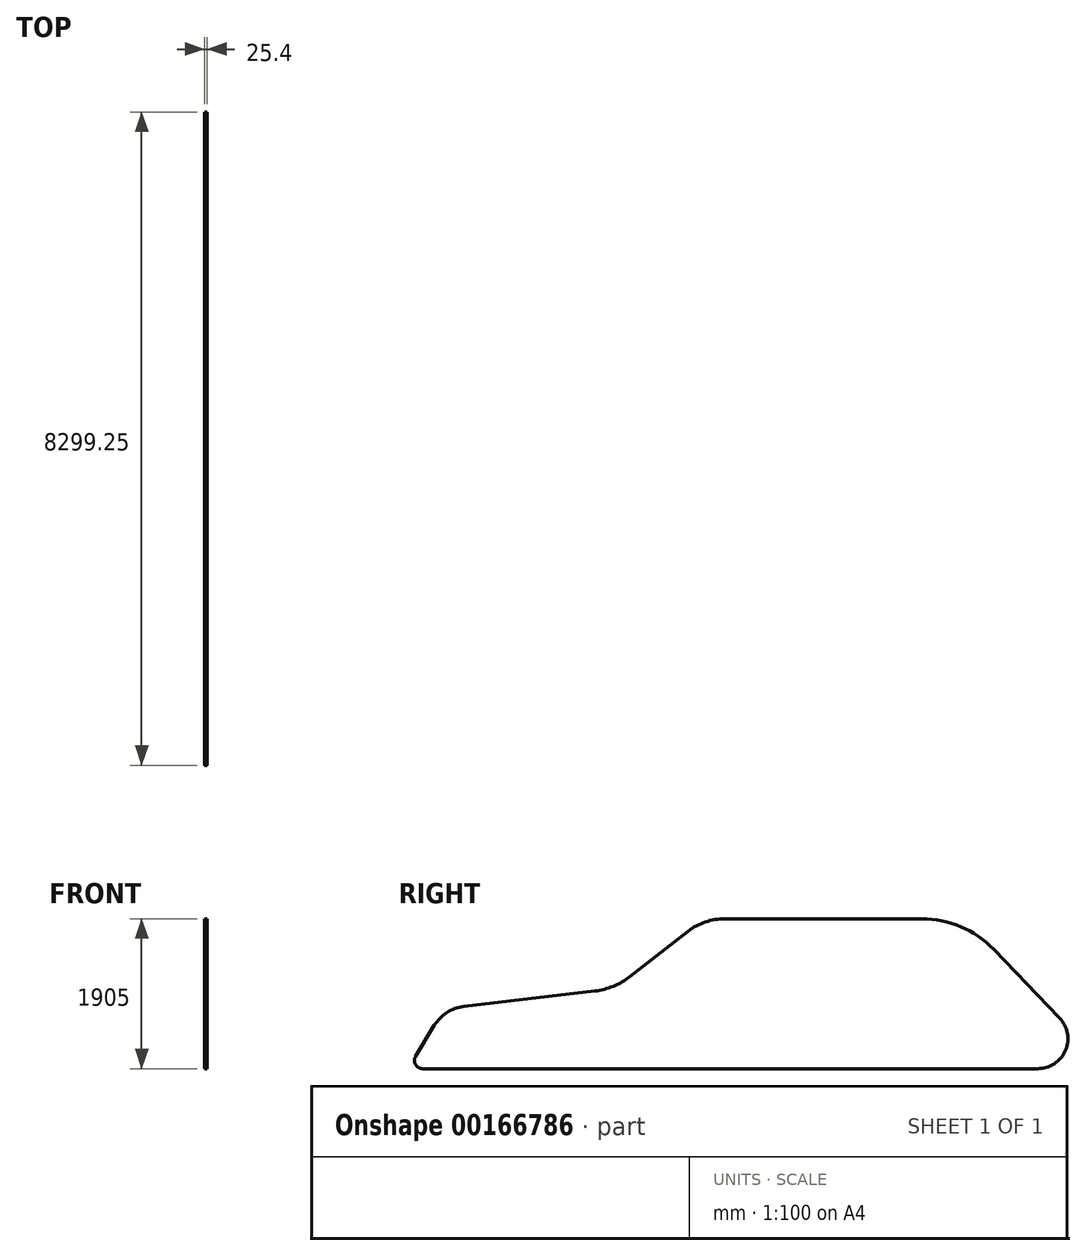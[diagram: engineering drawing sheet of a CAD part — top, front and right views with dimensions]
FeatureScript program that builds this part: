
annotation { "Feature Type Name" : "Feature", "Feature Type Description" : "" }
export const myFeature = defineFeature(function(context is Context, id is Id, definition is map)
    precondition{}
    {
        {
            var Q0;
            Q0=qCreatedBy(makeId("Front.planeOp"),FACE);
            var sketch = newSketch(context, id + "F0", { "sketchPlane" : qUnion([Q0])});
            skLineSegment(sketch, "E0", {"start": v(0, -1143) * mm, "end": v(1407.05, -1143) * mm, "construction": true});
            skLineSegment(sketch, "E1", {"start": v(494.4, 0) * mm, "end": v(1594.53, 0) * mm});
            skLineSegment(sketch, "E2.top", {"start": v(1109.62, -621.68) * mm, "end": v(1389.02, -621.68) * mm});
            skPoint(sketch, "E3.visualSharp", {"position": v(1057.47, -621.68) * mm});
            skLineSegment(sketch, "E4", {"start": v(1058.82, -529.74) * mm, "end": v(1058.82, -570.88) * mm});
            skPoint(sketch, "E5.visualSharp", {"position": v(1058.82, -621.68) * mm});
            skArc(sketch, "E5.filletArc", {"start": v(1058.82, -570.88) * mm, "mid": v(1073.7, -606.8) * mm, "end": v(1109.62, -621.68) * mm});
            skLineSegment(sketch, "E6", {"start": v(1439.82, -570.88) * mm, "end": v(1439.82, -529.74) * mm});
            skPoint(sketch, "E7.visualSharp", {"position": v(1439.82, -621.68) * mm});
            skArc(sketch, "E7.filletArc", {"start": v(1389.02, -621.68) * mm, "mid": v(1424.94, -606.8) * mm, "end": v(1439.82, -570.88) * mm});
            skPoint(sketch, "E8.visualSharp", {"position": v(1058.82, -489.77) * mm});
            skArc(sketch, "E9.filletArc", {"start": v(1109.62, -478.94) * mm, "mid": v(1073.7, -493.81) * mm, "end": v(1058.82, -529.74) * mm});
            skPoint(sketch, "E10.visualSharp", {"position": v(1439.82, -489.77) * mm});
            skArc(sketch, "E10.filletArc", {"start": v(1439.82, -529.74) * mm, "mid": v(1424.94, -493.81) * mm, "end": v(1389.02, -478.94) * mm});
            skArc(sketch, "E11", {"start": v(1389.02, -478.94) * mm, "mid": v(1249.32, -469.28) * mm, "end": v(1109.62, -478.94) * mm});
            skSolve(sketch);
        }
        {
            var Q0;
            Q0=qCreatedBy(makeId("Right.planeOp"),FACE);
            var sketch = newSketch(context, id + "F1", { "sketchPlane" : qUnion([Q0])});
            skLineSegment(sketch, "E12", {"start": v(179.44, 0) * mm, "end": v(7996.1, 0) * mm});
            skLineSegment(sketch, "E13", {"start": v(92.32, 153.87) * mm, "end": v(328.8, 548) * mm});
            skPoint(sketch, "E14.visualSharp", {"position": v(0, 0) * mm});
            skArc(sketch, "E14.filletArc", {"start": v(92.32, 153.87) * mm, "mid": v(91.03, 51.54) * mm, "end": v(179.44, 0) * mm});
            skLineSegment(sketch, "E15", {"start": v(705.05, 791.16) * mm, "end": v(2369.98, 987.03) * mm});
            skPoint(sketch, "E16.visualSharp", {"position": v(457.2, 762) * mm});
            skArc(sketch, "E16.filletArc", {"start": v(705.05, 791.16) * mm, "mid": v(488.68, 713.3) * mm, "end": v(328.8, 548) * mm});
            skLineSegment(sketch, "E17", {"start": v(2811.9, 1168.2) * mm, "end": v(3552.83, 1744.49) * mm});
            skPoint(sketch, "E18.visualSharp", {"position": v(2616.2, 1016) * mm});
            skArc(sketch, "E18.filletArc", {"start": v(2369.98, 987.03) * mm, "mid": v(2603.33, 1047.39) * mm, "end": v(2811.9, 1168.2) * mm});
            skLineSegment(sketch, "E19", {"start": v(4020.65, 1905) * mm, "end": v(6519.9, 1905) * mm});
            skPoint(sketch, "E20.visualSharp", {"position": v(3759.2, 1905) * mm});
            skArc(sketch, "E20.filletArc", {"start": v(4020.65, 1905) * mm, "mid": v(3773.35, 1863.76) * mm, "end": v(3552.83, 1744.49) * mm});
            skLineSegment(sketch, "E21", {"start": v(7436.07, 1514.52) * mm, "end": v(8270.94, 644.85) * mm});
            skPoint(sketch, "E22.visualSharp", {"position": v(7061.2, 1905) * mm});
            skArc(sketch, "E22.filletArc", {"start": v(7436.07, 1514.52) * mm, "mid": v(7017.86, 1803.3) * mm, "end": v(6519.9, 1905) * mm});
            skPoint(sketch, "E23.visualSharp", {"position": v(8890, 0) * mm});
            skArc(sketch, "E23.filletArc", {"start": v(7996.1, 0) * mm, "mid": v(8346.58, 231.61) * mm, "end": v(8270.94, 644.85) * mm});
            skSolve(sketch);
        }
        {
            var Q0;
            Q0=qSketchRegion(id+"F1",true);
            extrude(context, id + "F2", {"entities" : qUnion([Q0]), "depth" : 25.4 * mm});
        }
    });
